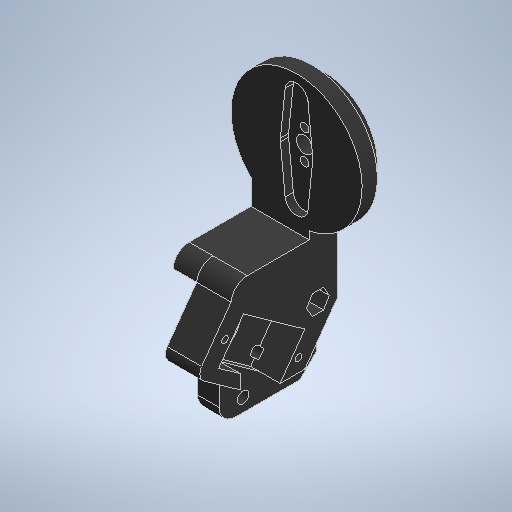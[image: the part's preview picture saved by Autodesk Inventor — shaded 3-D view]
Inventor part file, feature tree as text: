
AUTODESK INVENTOR PART (.ipt)
format: ipt  version: 2025.2 (Build 292293000, 293)  size: 549,376 bytes
history: native  units: mm
features: extrude x18, sketch x12, chamfer x3, fillet x2, projected_geometry x1
ambient origin geometry x8: Origin, YZ Plane, XZ Plane, XY Plane, X Axis, Y Axis, Z Axis, Center Point
bodies: Solid4 (feature_tree)
feature tree (36):
  extrude  "Extrusion48"  Depth=8.65mm TaperAngle=0.0deg
  sketch  "Sketch49"  dims[d338=5.0mm d339=9.0mm]
  extrude  "Extrusion52"  Depth=5.0mm
  extrude  "Extrusion53"  Depth=8.65mm TaperAngle=0.0deg
  extrude  "Extrusion54"  Depth=28.0mm
  extrude  "Extrusion55"  Depth=2.5mm TaperAngle=0.0deg
  extrude  "Extrusion56"  Depth=3.0mm TaperAngle=0.0deg
  sketch  "Sketch55"  dims[d348=6.0mm d349=3.0mm d350=0.0mm]
  extrude  "Extrusion57"  Depth=5.0mm
  extrude  "Extrusion58"  Depth=22.0mm
  extrude  "Extrusion59"  Depth=40.5mm TaperAngle=0.0deg
  sketch  "Sketch56"  dims[d354=17.75mm d355=5.0mm]
  extrude  "Extrusion60"  Depth=10.0mm TaperAngle=0.0deg
  extrude  "Extrusion61"  Depth=3.0mm
  sketch  "Sketch57"  dims[d357=64.0mm d358=22.0mm]
  extrude  "Extrusion62"  Depth=5.0mm
  extrude  "Extrusion63"  Depth=5.0mm
  extrude  "Extrusion64"  Depth=5.0mm
  sketch  "Sketch59"  dims[d363=3.0mm d367=10.0mm d368=0.0mm]
  extrude  "Extrusion65"  Depth=5.0mm
  extrude  "Extrusion66"  Depth=5.0mm
  extrude  "Extrusion67"  Depth=5.0mm
  extrude  "Extrusion68"  Depth=5.0mm
  chamfer  "Chamfer5"  Distance=2.0mm
  chamfer  "Chamfer6"  Distance=24.0mm
  fillet  "Fillet12"  Radius=28.3616mm
  fillet  "Fillet13"  Radius=20.0mm
  chamfer  "Chamfer7"  Distance=7.25mm
  sketch  "Sketch45"  dims[d321=40.0mm d322=8.65mm d323=0.0mm]
  sketch  "Sketch50"  dims[d340=2.6mm d341=8.65mm d342=0.0mm]
  sketch  "Sketch52"  dims[d343=7.0mm d344=28.0mm]
  sketch  "Sketch54"  dims[d345=9.9mm d346=2.5mm d347=0.0mm]
  sketch  "Sketch58"  dims[d359=40.5mm d360=0.0mm d361=40.5mm d362=0.0mm]
  sketch  "Sketch60"  dims[d369=23.0mm d370=3.0mm]
  projected_geometry  "Projected Loop9"
  sketch  "Sketch61"  dims[d371=6.0mm d372=0.5mm d375=38.0mm d377=12.0mm d378=1.5mm d383=1.5mm d384=3.5mm d385=1.0mm d386=2.0mm d388=24.0mm d389=28.3616mm d392=20.0mm d393=7.25mm d394=0.0mm d395=0.0mm d396=0.0mm d397=32.5mm d398=25.2mm d399=3.0mm d400=21.9mm d402=15.0mm d403=0.0mm d404=0.0mm d405=10.0mm d406=0.0mm d407=3.5mm d408=14.0mm d409=60.0mm d410=18.0mm d413=3.3mm d414=13.0mm d415=45.0deg d416=4.65mm d417=0.0mm d418=0.0mm d419=0.0mm d420=6.0mm d421=6.5mm d422=0.0mm d423=13.0mm d424=23.0mm d427=2.3mm d428=2.0mm d429=3.5mm d430=6.0mm d431=9.0mm d432=0.0mm d433=10.0mm d434=0.0mm d437=13.0mm d438=0.0mm d439=0.0mm d440=6.5mm d441=0.0mm d442=1.0mm d443=2.0mm d444=45.0deg d445=5.0mm d446=2.0mm d447=45.0deg d448=5.0mm d449=5.0mm d450=4.0mm d451=2.0mm d452=45.0deg d252=0.0mm d253=0.0mm d254=0.0mm d255=0.0mm]
